# Revit family: 206_UFI-_
name_source: partatom
category: Duct Accessories
units: mm (PartAtom-declared; Revit-internal decimal feet)

## family parameters
Always vertical = Yes
Cut with Voids When Loaded = No
Part Type = Breaks Into
Round Connector Dimension = Use Diameter
Shared = No
Work Plane-Based = No

## types (8) — shared parameters
CAT0 = Yes
Description = DUCT FILTER
L = 70 mm  [stored 0.229659 ft]
L2D = 70 mm  [stored 0.229659 ft]
LL = 35 mm  [stored 0.114829 ft]
Manufacturer = Alnor
QmdConnectorList = 201;D;202;D
URL = http://www.ventilation-alnor.co.uk
magiPartTypeId = 206
magiProductFamilyId = UFI-*

## per-type parameters (varying)
| type | D | H2D | R | W2D |
| UFI-100 | 100 mm | 100 mm  [stored 0.328084 ft] | 50 mm  [stored 0.164042 ft] | 100 mm  [stored 0.328084 ft] |
| UFI-400 | 400 mm | 400 mm | 200 mm | 400 mm |
| UFI-355 | 355 mm | 355 mm | 178 mm | 355 mm |
| UFI-315 | 315 mm | 315 mm | 158 mm | 315 mm |
| UFI-250 | 250 mm | 250 mm | 125 mm | 250 mm |
| UFI-200 | 200 mm | 200 mm | 100 mm  [stored 0.328084 ft] | 200 mm |
| UFI-160 | 160 mm | 160 mm | 80 mm  [stored 0.262467 ft] | 160 mm |
| UFI-125 | 125 mm | 125 mm | 63 mm | 125 mm |

note: column(s) folded — value = type name in every type: MC Product Code, magiProductId

note: [stored X ft] marks values corroborated as IEEE doubles in the binary element streams (Revit-internal decimal feet)

## geometry (parser evidence)
native form markers: Blend x4, Sweep x3
no freeform markers — native parametric forms only
